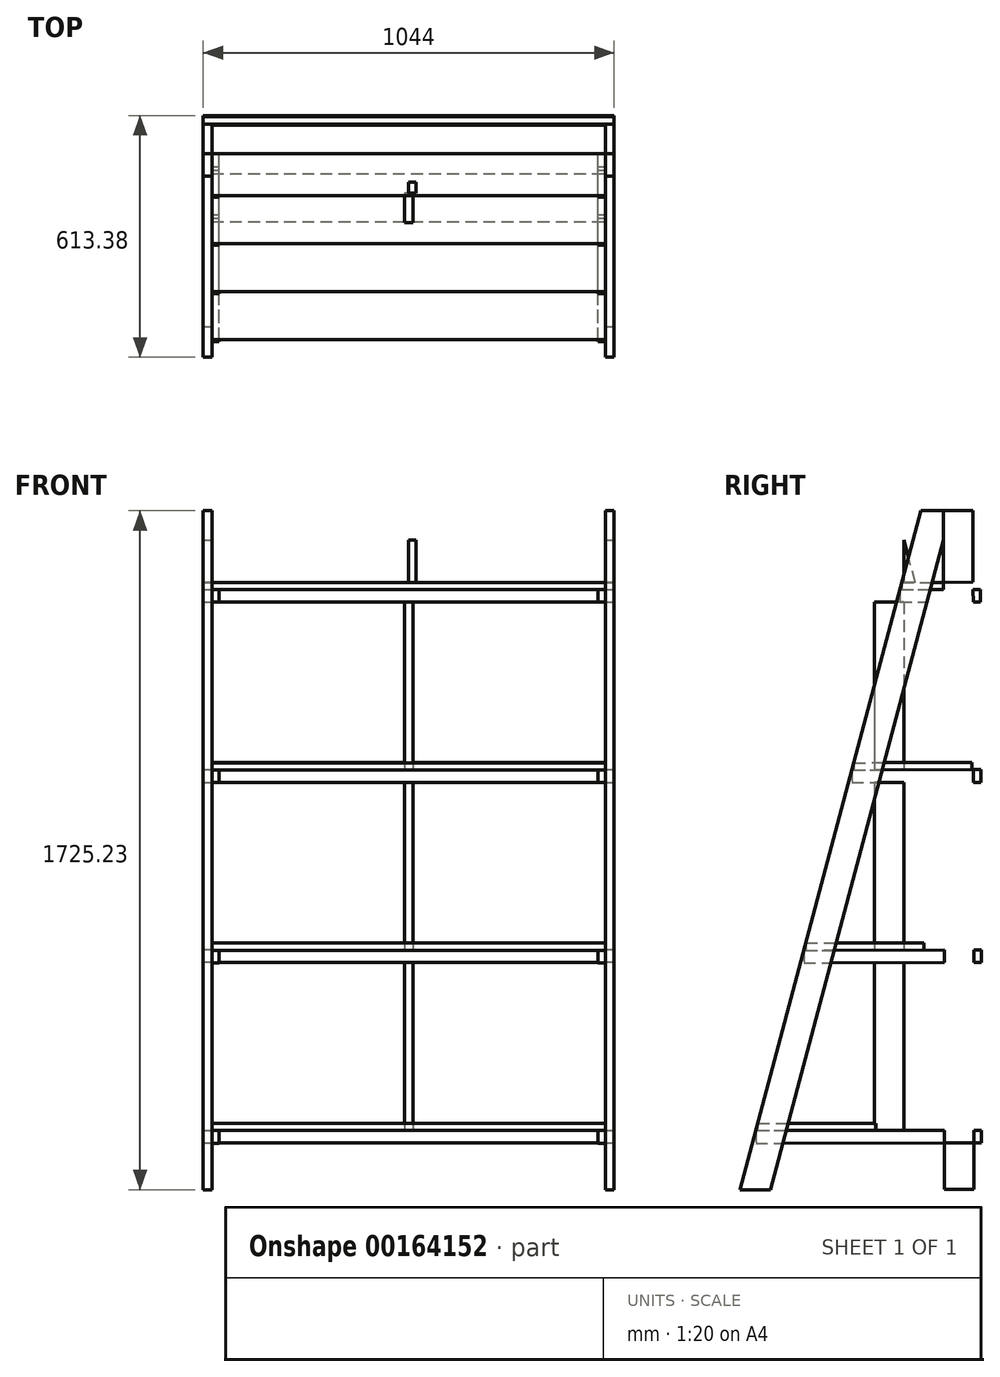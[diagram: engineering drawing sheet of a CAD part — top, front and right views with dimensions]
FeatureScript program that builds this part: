
annotation { "Feature Type Name" : "Feature", "Feature Type Description" : "" }
export const myFeature = defineFeature(function(context is Context, id is Id, definition is map)
    precondition{}
    {
        {
            var Q0;
            Q0=qCreatedBy(makeId("Right.planeOp"),FACE);
            var sketch = newSketch(context, id + "F0", { "sketchPlane" : qUnion([Q0])});
            skLineSegment(sketch, "E0.bottom", {"start": v(-125, 862.14) * mm, "end": v(-50, 862.14) * mm});
            skLineSegment(sketch, "E0.top", {"start": v(-125, -862.14) * mm, "end": v(-50, -862.14) * mm});
            skLineSegment(sketch, "E0.left", {"start": v(-125, 862.14) * mm, "end": v(-125, -862.14) * mm});
            skLineSegment(sketch, "E0.right", {"start": v(-50, 862.14) * mm, "end": v(-50, -862.14) * mm});
            skLineSegment(sketch, "E1", {"start": v(-50, 862.14) * mm, "end": v(7.55, 862.14) * mm});
            skLineSegment(sketch, "E2", {"start": v(7.55, 862.14) * mm, "end": v(469.57, -862.14) * mm});
            skLineSegment(sketch, "E3", {"start": v(469.57, -862.14) * mm, "end": v(391.92, -862.14) * mm});
            skLineSegment(sketch, "E4", {"start": v(391.92, -862.14) * mm, "end": v(-50, 787.14) * mm});
            skLineSegment(sketch, "E5", {"start": v(469.57, -862.14) * mm, "end": v(397.12, -881.55) * mm, "construction": true});
            skLineSegment(sketch, "E6", {"start": v(397.12, -881.55) * mm, "end": v(391.92, -862.14) * mm, "construction": true});
            skLineSegment(sketch, "E7", {"start": v(391.92, -862.14) * mm, "end": v(397.12, -881.55) * mm, "construction": true});
            skLineSegment(sketch, "E8", {"start": v(-50, 787.14) * mm, "end": v(-68.75, 857.12) * mm, "construction": true});
            skLineSegment(sketch, "E9", {"start": v(3.7, 876.53) * mm, "end": v(7.55, 862.14) * mm, "construction": true});
            skLineSegment(sketch, "E10", {"start": v(-68.75, 857.12) * mm, "end": v(-50, 862.14) * mm, "construction": true});
            skLineSegment(sketch, "E11", {"start": v(-50, 862.14) * mm, "end": v(3.7, 876.53) * mm, "construction": true});
            skPoint(sketch, "E12", {"position": v(-50, 0) * mm});
            skLineSegment(sketch, "E13", {"start": v(-50, 0) * mm, "end": v(0, 0) * mm, "construction": true});
            skLineSegment(sketch, "E14", {"start": v(-125, -712.14) * mm, "end": v(429.38, -712.14) * mm, "construction": true});
            skLineSegment(sketch, "E15.bottom", {"start": v(424.55, -694.14) * mm, "end": v(124.55, -694.14) * mm});
            skLineSegment(sketch, "E15.top", {"start": v(424.55, -712.14) * mm, "end": v(124.55, -712.14) * mm});
            skLineSegment(sketch, "E15.left", {"start": v(424.55, -694.14) * mm, "end": v(424.55, -712.14) * mm});
            skLineSegment(sketch, "E15.right", {"start": v(124.55, -694.14) * mm, "end": v(124.55, -712.14) * mm});
            skLineSegment(sketch, "E16", {"start": v(-125, -712.14) * mm, "end": v(-125, -254.05) * mm, "construction": true});
            skLineSegment(sketch, "E17", {"start": v(-125, -254.05) * mm, "end": v(306.63, -254.05) * mm, "construction": true});
            skLineSegment(sketch, "E18", {"start": v(-125, -254.05) * mm, "end": v(-125, 204.05) * mm, "construction": true});
            skLineSegment(sketch, "E19", {"start": v(-125, 204.05) * mm, "end": v(183.89, 204.05) * mm, "construction": true});
            skLineSegment(sketch, "E20", {"start": v(-125, 662.14) * mm, "end": v(61.14, 662.14) * mm, "construction": true});
            skLineSegment(sketch, "E21", {"start": v(-125, 662.14) * mm, "end": v(-125, 204.05) * mm, "construction": true});
            skLineSegment(sketch, "E22.bottom", {"start": v(301.8, -236.05) * mm, "end": v(1.8, -236.05) * mm});
            skLineSegment(sketch, "E22.top", {"start": v(301.8, -254.05) * mm, "end": v(1.8, -254.05) * mm});
            skLineSegment(sketch, "E22.left", {"start": v(301.8, -236.05) * mm, "end": v(301.8, -254.05) * mm});
            skLineSegment(sketch, "E22.right", {"start": v(1.8, -236.05) * mm, "end": v(1.8, -254.05) * mm});
            skLineSegment(sketch, "E23.bottom", {"start": v(179.06, 222.05) * mm, "end": v(-120.94, 222.05) * mm});
            skLineSegment(sketch, "E23.top", {"start": v(179.06, 204.05) * mm, "end": v(-120.94, 204.05) * mm});
            skLineSegment(sketch, "E23.left", {"start": v(179.06, 222.05) * mm, "end": v(179.06, 204.05) * mm});
            skLineSegment(sketch, "E23.right", {"start": v(-120.94, 222.05) * mm, "end": v(-120.94, 204.05) * mm});
            skLineSegment(sketch, "E24.bottom", {"start": v(56.32, 680.14) * mm, "end": v(-125, 680.14) * mm});
            skLineSegment(sketch, "E24.top", {"start": v(56.32, 662.14) * mm, "end": v(-125, 662.14) * mm});
            skLineSegment(sketch, "E24.left", {"start": v(56.32, 680.14) * mm, "end": v(56.32, 662.14) * mm});
            skLineSegment(sketch, "E24.right", {"start": v(-125, 680.14) * mm, "end": v(-125, 662.14) * mm});
            skLineSegment(sketch, "E25.bottom", {"start": v(429.38, -712.14) * mm, "end": v(-125, -712.14) * mm});
            skLineSegment(sketch, "E25.top", {"start": v(429.38, -744.14) * mm, "end": v(-125, -744.14) * mm});
            skLineSegment(sketch, "E25.left", {"start": v(429.38, -712.14) * mm, "end": v(429.38, -744.14) * mm});
            skLineSegment(sketch, "E25.right", {"start": v(-125, -712.14) * mm, "end": v(-125, -744.14) * mm});
            skLineSegment(sketch, "E26.bottom", {"start": v(306.63, -254.05) * mm, "end": v(-125, -254.05) * mm});
            skLineSegment(sketch, "E26.top", {"start": v(306.63, -286.05) * mm, "end": v(-125, -286.05) * mm});
            skLineSegment(sketch, "E26.left", {"start": v(306.63, -254.05) * mm, "end": v(306.63, -286.05) * mm});
            skLineSegment(sketch, "E26.right", {"start": v(-125, -254.05) * mm, "end": v(-125, -286.05) * mm});
            skLineSegment(sketch, "E27.bottom", {"start": v(183.89, 204.05) * mm, "end": v(-125, 204.05) * mm});
            skLineSegment(sketch, "E27.top", {"start": v(183.89, 172.05) * mm, "end": v(-125, 172.05) * mm});
            skLineSegment(sketch, "E27.left", {"start": v(183.89, 204.05) * mm, "end": v(183.89, 172.05) * mm});
            skLineSegment(sketch, "E27.right", {"start": v(-125, 204.05) * mm, "end": v(-125, 172.05) * mm});
            skLineSegment(sketch, "E28.bottom", {"start": v(61.14, 662.14) * mm, "end": v(-125, 662.14) * mm});
            skLineSegment(sketch, "E28.top", {"start": v(61.14, 630.14) * mm, "end": v(-125, 630.14) * mm});
            skLineSegment(sketch, "E28.left", {"start": v(61.14, 662.14) * mm, "end": v(61.14, 630.14) * mm});
            skLineSegment(sketch, "E28.right", {"start": v(-125, 662.14) * mm, "end": v(-125, 630.14) * mm});
            skLineSegment(sketch, "E29", {"start": v(0, 1113.68) * mm, "end": v(1.8, -1143.74) * mm, "construction": true});
            skSolve(sketch);
        }
        {
            var Q0;
            {var subQ0=sQuery(id+"F0.wireOp",EDGE,"E27.left");Q0=makeQuery(id+"F0.imprint","IMPRINT",FACE,{"disambiguationData":[TD([[makeQuery(id+"F0.imprint","IMPRINT",EDGE,{"derivedFrom":subQ0}),-1.0]])]});}
            var Q1;
            {var subQ0=sQuery(id+"F0.wireOp",EDGE,"E27.left");Q1=makeQuery(id+"F0.imprint","IMPRINT",FACE,{"disambiguationData":[TD([[makeQuery(id+"F0.imprint","IMPRINT",EDGE,{"derivedFrom":subQ0}),1.0]])]});}
            var Q2;
            {var subQ0=sQuery(id+"F0.wireOp",EDGE,"E23.left");Q2=makeQuery(id+"F0.imprint","IMPRINT",FACE,{"disambiguationData":[TD([[makeQuery(id+"F0.imprint","IMPRINT",EDGE,{"derivedFrom":subQ0}),1.0]])]});}
            var Q3;
            {var subQ5=sQuery(id+"F0.wireOp",EDGE,"E23.left");Q3=makeQuery(id+"F0.imprint","IMPRINT",FACE,{"disambiguationData":[TD([[makeQuery(id+"F0.imprint","IMPRINT",EDGE,{"derivedFrom":subQ5}),-1.0]])]});}
            var Q4;
            {var subQ0=sQuery(id+"F0.wireOp",EDGE,"E28.left");Q4=makeQuery(id+"F0.imprint","IMPRINT",FACE,{"disambiguationData":[TD([[makeQuery(id+"F0.imprint","IMPRINT",EDGE,{"derivedFrom":subQ0}),1.0]])]});}
            var Q5;
            {var subQ0=sQuery(id+"F0.wireOp",EDGE,"E26.left");Q5=makeQuery(id+"F0.imprint","IMPRINT",FACE,{"disambiguationData":[TD([[makeQuery(id+"F0.imprint","IMPRINT",EDGE,{"derivedFrom":subQ0}),1.0]])]});}
            var Q6;
            {var subQ0=sQuery(id+"F0.wireOp",EDGE,"E26.left");Q6=makeQuery(id+"F0.imprint","IMPRINT",FACE,{"disambiguationData":[TD([[makeQuery(id+"F0.imprint","IMPRINT",EDGE,{"derivedFrom":subQ0}),-1.0]])]});}
            var Q7;
            {var subQ5=sQuery(id+"F0.wireOp",EDGE,"E22.left");Q7=makeQuery(id+"F0.imprint","IMPRINT",FACE,{"disambiguationData":[TD([[makeQuery(id+"F0.imprint","IMPRINT",EDGE,{"derivedFrom":subQ5}),-1.0]])]});}
            var Q8;
            {var subQ0=sQuery(id+"F0.wireOp",EDGE,"E22.left");Q8=makeQuery(id+"F0.imprint","IMPRINT",FACE,{"disambiguationData":[TD([[makeQuery(id+"F0.imprint","IMPRINT",EDGE,{"derivedFrom":subQ0}),1.0]])]});}
            var Q9;
            {var subQ4=sQuery(id+"F0.wireOp",EDGE,"E3");Q9=makeQuery(id+"F0.imprint","IMPRINT",FACE,{"disambiguationData":[TD([[makeQuery(id+"F0.imprint","IMPRINT",EDGE,{"derivedFrom":subQ4}),-1.0]])]});}
            var Q10;
            {var subQ4=sQuery(id+"F0.wireOp",EDGE,"E25.left");Q10=makeQuery(id+"F0.imprint","IMPRINT",FACE,{"disambiguationData":[TD([[makeQuery(id+"F0.imprint","IMPRINT",EDGE,{"derivedFrom":subQ4}),-1.0]])]});}
            var Q11;
            {var subQ5=sQuery(id+"F0.wireOp",EDGE,"E15.left");Q11=makeQuery(id+"F0.imprint","IMPRINT",FACE,{"disambiguationData":[TD([[makeQuery(id+"F0.imprint","IMPRINT",EDGE,{"derivedFrom":subQ5}),-1.0]])]});}
            var Q12;
            {var subQ0=sQuery(id+"F0.wireOp",EDGE,"E15.left");Q12=makeQuery(id+"F0.imprint","IMPRINT",FACE,{"disambiguationData":[TD([[makeQuery(id+"F0.imprint","IMPRINT",EDGE,{"derivedFrom":subQ0}),1.0]])]});}
            var Q13;
            {var subQ1=sQuery(id+"F0.wireOp",EDGE,"E2");var subQ3=sQuery(id+"F0.wireOp",EDGE,"q1gE5B2j-BdVa-rHxn-HZzA-WCDaylD2YWi6");var subQ4=makeQuery(id+"F0.imprint","INTERSECT",VERTEX,{"derivedFrom":[subQ1,subQ3]});Q13=makeQuery(id+"F0.imprint","IMPRINT",FACE,{"disambiguationData":[TD([[makeQuery(id+"F0.imprint","IMPRINT",EDGE,{"disambiguationData":[TD([[subQ4,-1.0]])],"derivedFrom":subQ1}),-1.0]])]});}
            var Q14;
            {var subQ0=sQuery(id+"F0.wireOp",EDGE,"E1");Q14=makeQuery(id+"F0.imprint","IMPRINT",FACE,{"disambiguationData":[TD([[makeQuery(id+"F0.imprint","IMPRINT",EDGE,{"derivedFrom":subQ0}),-1.0]])]});}
            var Q15;
            {var subQ5=sQuery(id+"F0.wireOp",EDGE,"E24.left");Q15=makeQuery(id+"F0.imprint","IMPRINT",FACE,{"disambiguationData":[TD([[makeQuery(id+"F0.imprint","IMPRINT",EDGE,{"derivedFrom":subQ5}),-1.0]])]});}
            var Q16;
            {var subQ0=sQuery(id+"F0.wireOp",EDGE,"E28.left");Q16=makeQuery(id+"F0.imprint","IMPRINT",FACE,{"disambiguationData":[TD([[makeQuery(id+"F0.imprint","IMPRINT",EDGE,{"derivedFrom":subQ0}),-1.0]])]});}
            var Q17;
            {var subQ0=sQuery(id+"F0.wireOp",EDGE,"E24.left");Q17=makeQuery(id+"F0.imprint","IMPRINT",FACE,{"disambiguationData":[TD([[makeQuery(id+"F0.imprint","IMPRINT",EDGE,{"derivedFrom":subQ0}),1.0]])]});}
            extrude(context, id + "F1", {"entities" : qUnion([Q0, Q1, Q2, Q3, Q4, Q5, Q6, Q7, Q8, Q9, Q10, Q11, Q12, Q13, Q14, Q15, Q16, Q17]), "depth" : 11 * mm, "hasSecondDirection" : true, "secondDirectionOppositeDirection" : true, "secondDirectionDepth" : 11 * mm});
        }
        {
            var Q0;
            {var subQ4=sQuery(id+"F0.wireOp",EDGE,"E0.bottom");Q0=makeQuery(id+"F0.imprint","IMPRINT",FACE,{"disambiguationData":[TD([[makeQuery(id+"F0.imprint","IMPRINT",EDGE,{"derivedFrom":subQ4}),-1.0]])]});}
            var Q1;
            {var subQ5=sQuery(id+"F0.wireOp",EDGE,"E24.right");Q1=makeQuery(id+"F0.imprint","IMPRINT",FACE,{"disambiguationData":[TD([[makeQuery(id+"F0.imprint","IMPRINT",EDGE,{"derivedFrom":subQ5}),1.0]])]});}
            var Q2;
            {var subQ5=sQuery(id+"F0.wireOp",EDGE,"E23.right");Q2=makeQuery(id+"F0.imprint","IMPRINT",FACE,{"disambiguationData":[TD([[makeQuery(id+"F0.imprint","IMPRINT",EDGE,{"derivedFrom":subQ5}),-1.0]])]});}
            var Q3;
            {var subQ5=sQuery(id+"F0.wireOp",EDGE,"E28.right");Q3=makeQuery(id+"F0.imprint","IMPRINT",FACE,{"disambiguationData":[TD([[makeQuery(id+"F0.imprint","IMPRINT",EDGE,{"derivedFrom":subQ5}),1.0]])]});}
            var Q4;
            {var subQ2=sQuery(id+"F0.wireOp",EDGE,"E27.right");Q4=makeQuery(id+"F0.imprint","IMPRINT",FACE,{"disambiguationData":[TD([[makeQuery(id+"F0.imprint","IMPRINT",EDGE,{"derivedFrom":subQ2}),1.0]])]});}
            var Q5;
            {var subQ5=sQuery(id+"F0.wireOp",EDGE,"E23.right");Q5=makeQuery(id+"F0.imprint","IMPRINT",FACE,{"disambiguationData":[TD([[makeQuery(id+"F0.imprint","IMPRINT",EDGE,{"derivedFrom":subQ5}),1.0]])]});}
            var Q6;
            {var subQ3=sQuery(id+"F0.wireOp",EDGE,"E27.top");var subQ5=sQuery(id+"F0.wireOp",EDGE,"E0.right");var subQ6=makeQuery(id+"F0.imprint","INTERSECT",VERTEX,{"derivedFrom":[subQ5,subQ3]});Q6=makeQuery(id+"F0.imprint","IMPRINT",FACE,{"disambiguationData":[TD([[makeQuery(id+"F0.imprint","IMPRINT",EDGE,{"disambiguationData":[TD([[subQ6,-1.0]])],"derivedFrom":subQ5}),-1.0]])]});}
            var Q7;
            {var subQ5=sQuery(id+"F0.wireOp",EDGE,"E26.right");Q7=makeQuery(id+"F0.imprint","IMPRINT",FACE,{"disambiguationData":[TD([[makeQuery(id+"F0.imprint","IMPRINT",EDGE,{"derivedFrom":subQ5}),1.0]])]});}
            var Q8;
            {var subQ3=sQuery(id+"F0.wireOp",EDGE,"E26.top");var subQ5=sQuery(id+"F0.wireOp",EDGE,"E0.right");var subQ7=makeQuery(id+"F0.imprint","INTERSECT",VERTEX,{"derivedFrom":[subQ5,subQ3]});Q8=makeQuery(id+"F0.imprint","IMPRINT",FACE,{"disambiguationData":[TD([[makeQuery(id+"F0.imprint","IMPRINT",EDGE,{"disambiguationData":[TD([[subQ7,-1.0]])],"derivedFrom":subQ5}),-1.0]])]});}
            var Q9;
            {var subQ5=sQuery(id+"F0.wireOp",EDGE,"E25.right");Q9=makeQuery(id+"F0.imprint","IMPRINT",FACE,{"disambiguationData":[TD([[makeQuery(id+"F0.imprint","IMPRINT",EDGE,{"derivedFrom":subQ5}),1.0]])]});}
            var Q10;
            {var subQ0=sQuery(id+"F0.wireOp",EDGE,"E0.top");Q10=makeQuery(id+"F0.imprint","IMPRINT",FACE,{"disambiguationData":[TD([[makeQuery(id+"F0.imprint","IMPRINT",EDGE,{"derivedFrom":subQ0}),1.0]])]});}
            extrude(context, id + "F2", {"entities" : qUnion([Q0, Q1, Q2, Q3, Q4, Q5, Q6, Q7, Q8, Q9, Q10]), "depth" : 11 * mm, "hasSecondDirection" : true, "secondDirectionOppositeDirection" : true, "secondDirectionDepth" : 11 * mm});
        }
        {
            var Q0;
            Q0=makeQuery(id+"F1.opExtrude","SWEPT_BODY",BODY,{"disambiguationData":[OSD([sQuery(id+"F0.wireOp",EDGE,"E0.bottom"),sQuery(id+"F0.wireOp",EDGE,"E0.top"),sQuery(id+"F0.wireOp",EDGE,"E0.left"),sQuery(id+"F0.wireOp",EDGE,"E0.right"),sQuery(id+"F0.wireOp",EDGE,"E1"),sQuery(id+"F0.wireOp",EDGE,"E2"),sQuery(id+"F0.wireOp",EDGE,"E3"),sQuery(id+"F0.wireOp",EDGE,"E4"),sQuery(id+"F0.wireOp",EDGE,"E24.right"),sQuery(id+"F0.wireOp",EDGE,"E25.right"),sQuery(id+"F0.wireOp",EDGE,"E26.right"),sQuery(id+"F0.wireOp",EDGE,"E27.right"),sQuery(id+"F0.wireOp",EDGE,"E28.right")])]});
            var Q1;
            Q1=makeQuery(id+"F2.opExtrude","SWEPT_BODY",BODY,{"disambiguationData":[OSD([sQuery(id+"F0.wireOp",EDGE,"E0.bottom"),sQuery(id+"F0.wireOp",EDGE,"E0.top"),sQuery(id+"F0.wireOp",EDGE,"E0.left"),sQuery(id+"F0.wireOp",EDGE,"E0.right"),sQuery(id+"F0.wireOp",EDGE,"E24.right"),sQuery(id+"F0.wireOp",EDGE,"E25.right"),sQuery(id+"F0.wireOp",EDGE,"E26.right"),sQuery(id+"F0.wireOp",EDGE,"E27.right"),sQuery(id+"F0.wireOp",EDGE,"E28.right")])]});
            transform(context, id + "F3", {"entities" : qUnion([Q0, Q1]), "transformType" : TransformType.TRANSLATION_3D, "dx" : 511 * mm, "dy" : 0 * mm, "dz" : 0 * mm, "makeCopy" : false});
        }
        {
            var Q0;
            Q0=makeQuery(id+"F1.opExtrude","SWEPT_BODY",BODY,{"disambiguationData":[OSD([sQuery(id+"F0.wireOp",EDGE,"E0.bottom"),sQuery(id+"F0.wireOp",EDGE,"E0.top"),sQuery(id+"F0.wireOp",EDGE,"E0.left"),sQuery(id+"F0.wireOp",EDGE,"E0.right"),sQuery(id+"F0.wireOp",EDGE,"E1"),sQuery(id+"F0.wireOp",EDGE,"E2"),sQuery(id+"F0.wireOp",EDGE,"E3"),sQuery(id+"F0.wireOp",EDGE,"E4"),sQuery(id+"F0.wireOp",EDGE,"E24.right"),sQuery(id+"F0.wireOp",EDGE,"E25.right"),sQuery(id+"F0.wireOp",EDGE,"E26.right"),sQuery(id+"F0.wireOp",EDGE,"E27.right"),sQuery(id+"F0.wireOp",EDGE,"E28.right")])]});
            var Q1;
            Q1=makeQuery(id+"F2.opExtrude","SWEPT_BODY",BODY,{"disambiguationData":[OSD([sQuery(id+"F0.wireOp",EDGE,"E0.bottom"),sQuery(id+"F0.wireOp",EDGE,"E0.top"),sQuery(id+"F0.wireOp",EDGE,"E0.left"),sQuery(id+"F0.wireOp",EDGE,"E0.right"),sQuery(id+"F0.wireOp",EDGE,"E24.right"),sQuery(id+"F0.wireOp",EDGE,"E25.right"),sQuery(id+"F0.wireOp",EDGE,"E26.right"),sQuery(id+"F0.wireOp",EDGE,"E27.right"),sQuery(id+"F0.wireOp",EDGE,"E28.right")])]});
            transform(context, id + "F4", {"entities" : qUnion([Q0, Q1]), "transformType" : TransformType.TRANSLATION_3D, "dx" : -1022 * mm, "dy" : 0 * mm, "dz" : 0 * mm, "makeCopy" : true});
        }
        {
            var Q0;
            {var subQ2=sQuery(id+"F0.wireOp",EDGE,"E0.right");var subQ6=sQuery(id+"F0.wireOp",EDGE,"E25.top");var subQ8=makeQuery(id+"F0.imprint","INTERSECT",VERTEX,{"derivedFrom":[subQ2,subQ6]});Q0=makeQuery(id+"F0.imprint","IMPRINT",FACE,{"disambiguationData":[TD([[makeQuery(id+"F0.imprint","IMPRINT",EDGE,{"disambiguationData":[TD([[subQ8,1.0]])],"derivedFrom":subQ2}),1.0]])]});}
            var Q1;
            {var subQ5=sQuery(id+"F0.wireOp",EDGE,"E25.right");Q1=makeQuery(id+"F0.imprint","IMPRINT",FACE,{"disambiguationData":[TD([[makeQuery(id+"F0.imprint","IMPRINT",EDGE,{"derivedFrom":subQ5}),1.0]])]});}
            var Q2;
            {var subQ4=sQuery(id+"F0.wireOp",EDGE,"E25.left");Q2=makeQuery(id+"F0.imprint","IMPRINT",FACE,{"disambiguationData":[TD([[makeQuery(id+"F0.imprint","IMPRINT",EDGE,{"derivedFrom":subQ4}),-1.0]])]});}
            var Q3;
            {var subQ0=sQuery(id+"F0.wireOp",EDGE,"E26.left");Q3=makeQuery(id+"F0.imprint","IMPRINT",FACE,{"disambiguationData":[TD([[makeQuery(id+"F0.imprint","IMPRINT",EDGE,{"derivedFrom":subQ0}),-1.0]])]});}
            var Q4;
            {var subQ0=sQuery(id+"F0.wireOp",EDGE,"E26.bottom");var subQ2=sQuery(id+"F0.wireOp",EDGE,"E0.right");var subQ3=makeQuery(id+"F0.imprint","INTERSECT",VERTEX,{"derivedFrom":[subQ2,subQ0]});Q4=makeQuery(id+"F0.imprint","IMPRINT",FACE,{"disambiguationData":[TD([[makeQuery(id+"F0.imprint","IMPRINT",EDGE,{"disambiguationData":[TD([[subQ3,-1.0]])],"derivedFrom":subQ2}),1.0]])]});}
            var Q5;
            {var subQ5=sQuery(id+"F0.wireOp",EDGE,"E26.right");Q5=makeQuery(id+"F0.imprint","IMPRINT",FACE,{"disambiguationData":[TD([[makeQuery(id+"F0.imprint","IMPRINT",EDGE,{"derivedFrom":subQ5}),1.0]])]});}
            var Q6;
            {var subQ2=sQuery(id+"F0.wireOp",EDGE,"E27.right");Q6=makeQuery(id+"F0.imprint","IMPRINT",FACE,{"disambiguationData":[TD([[makeQuery(id+"F0.imprint","IMPRINT",EDGE,{"derivedFrom":subQ2}),1.0]])]});}
            var Q7;
            {var subQ0=sQuery(id+"F0.wireOp",EDGE,"E27.bottom");var subQ1=sQuery(id+"F0.wireOp",EDGE,"E0.right");var subQ2=makeQuery(id+"F0.imprint","INTERSECT",VERTEX,{"derivedFrom":[subQ1,subQ0]});Q7=makeQuery(id+"F0.imprint","IMPRINT",FACE,{"disambiguationData":[TD([[makeQuery(id+"F0.imprint","IMPRINT",EDGE,{"disambiguationData":[TD([[subQ2,-1.0]])],"derivedFrom":subQ1}),1.0]])]});}
            var Q8;
            {var subQ0=sQuery(id+"F0.wireOp",EDGE,"E27.left");Q8=makeQuery(id+"F0.imprint","IMPRINT",FACE,{"disambiguationData":[TD([[makeQuery(id+"F0.imprint","IMPRINT",EDGE,{"derivedFrom":subQ0}),-1.0]])]});}
            var Q9;
            {var subQ5=sQuery(id+"F0.wireOp",EDGE,"E28.right");Q9=makeQuery(id+"F0.imprint","IMPRINT",FACE,{"disambiguationData":[TD([[makeQuery(id+"F0.imprint","IMPRINT",EDGE,{"derivedFrom":subQ5}),1.0]])]});}
            var Q10;
            {var subQ0=sQuery(id+"F0.wireOp",EDGE,"E28.bottom");var subQ1=sQuery(id+"F0.wireOp",EDGE,"E0.right");var subQ2=makeQuery(id+"F0.imprint","INTERSECT",VERTEX,{"derivedFrom":[subQ1,subQ0]});Q10=makeQuery(id+"F0.imprint","IMPRINT",FACE,{"disambiguationData":[TD([[makeQuery(id+"F0.imprint","IMPRINT",EDGE,{"disambiguationData":[TD([[subQ2,-1.0]])],"derivedFrom":subQ1}),1.0]])]});}
            var Q11;
            {var subQ0=sQuery(id+"F0.wireOp",EDGE,"E28.left");Q11=makeQuery(id+"F0.imprint","IMPRINT",FACE,{"disambiguationData":[TD([[makeQuery(id+"F0.imprint","IMPRINT",EDGE,{"derivedFrom":subQ0}),-1.0]])]});}
            extrude(context, id + "F5", {"entities" : qUnion([Q0, Q1, Q2, Q3, Q4, Q5, Q6, Q7, Q8, Q9, Q10, Q11]), "depth" : 19 * mm});
        }
        {
            var Q0;
            Q0=makeQuery(id+"F5.opExtrude","SWEPT_BODY",BODY,{"disambiguationData":[OSD([sQuery(id+"F0.wireOp",EDGE,"E28.bottom"),sQuery(id+"F0.wireOp",EDGE,"E28.top"),sQuery(id+"F0.wireOp",EDGE,"E28.left"),sQuery(id+"F0.wireOp",EDGE,"E28.right")])]});
            var Q1;
            Q1=makeQuery(id+"F5.opExtrude","SWEPT_BODY",BODY,{"disambiguationData":[OSD([sQuery(id+"F0.wireOp",EDGE,"E27.bottom"),sQuery(id+"F0.wireOp",EDGE,"E27.top"),sQuery(id+"F0.wireOp",EDGE,"E27.left"),sQuery(id+"F0.wireOp",EDGE,"E27.right")])]});
            var Q2;
            Q2=makeQuery(id+"F5.opExtrude","SWEPT_BODY",BODY,{"disambiguationData":[OSD([sQuery(id+"F0.wireOp",EDGE,"E26.bottom"),sQuery(id+"F0.wireOp",EDGE,"E26.top"),sQuery(id+"F0.wireOp",EDGE,"E26.left"),sQuery(id+"F0.wireOp",EDGE,"E26.right")])]});
            var Q3;
            Q3=makeQuery(id+"F5.opExtrude","SWEPT_BODY",BODY,{"disambiguationData":[OSD([sQuery(id+"F0.wireOp",EDGE,"E25.bottom"),sQuery(id+"F0.wireOp",EDGE,"E25.top"),sQuery(id+"F0.wireOp",EDGE,"E25.left"),sQuery(id+"F0.wireOp",EDGE,"E25.right")])]});
            transform(context, id + "F6", {"entities" : qUnion([Q0, Q1, Q2, Q3]), "transformType" : TransformType.TRANSLATION_3D, "dx" : -500 * mm, "dy" : 0 * mm, "dz" : 0 * mm, "makeCopy" : false});
        }
        {
            var Q0;
            Q0=makeQuery(id+"F5.opExtrude","SWEPT_BODY",BODY,{"disambiguationData":[OSD([sQuery(id+"F0.wireOp",EDGE,"E27.bottom"),sQuery(id+"F0.wireOp",EDGE,"E27.top"),sQuery(id+"F0.wireOp",EDGE,"E27.left"),sQuery(id+"F0.wireOp",EDGE,"E27.right")])]});
            var Q1;
            Q1=makeQuery(id+"F5.opExtrude","SWEPT_BODY",BODY,{"disambiguationData":[OSD([sQuery(id+"F0.wireOp",EDGE,"E28.bottom"),sQuery(id+"F0.wireOp",EDGE,"E28.top"),sQuery(id+"F0.wireOp",EDGE,"E28.left"),sQuery(id+"F0.wireOp",EDGE,"E28.right")])]});
            var Q2;
            Q2=makeQuery(id+"F5.opExtrude","SWEPT_BODY",BODY,{"disambiguationData":[OSD([sQuery(id+"F0.wireOp",EDGE,"E26.bottom"),sQuery(id+"F0.wireOp",EDGE,"E26.top"),sQuery(id+"F0.wireOp",EDGE,"E26.left"),sQuery(id+"F0.wireOp",EDGE,"E26.right")])]});
            var Q3;
            Q3=makeQuery(id+"F5.opExtrude","SWEPT_BODY",BODY,{"disambiguationData":[OSD([sQuery(id+"F0.wireOp",EDGE,"E25.bottom"),sQuery(id+"F0.wireOp",EDGE,"E25.top"),sQuery(id+"F0.wireOp",EDGE,"E25.left"),sQuery(id+"F0.wireOp",EDGE,"E25.right")])]});
            transform(context, id + "F7", {"entities" : qUnion([Q0, Q1, Q2, Q3]), "transformType" : TransformType.TRANSLATION_3D, "dx" : 981 * mm, "dy" : 0 * mm, "dz" : 0 * mm, "makeCopy" : true});
        }
        {
            var Q0;
            {var subQ0=sQuery(id+"F0.wireOp",EDGE,"E24.bottom");var subQ1=sQuery(id+"F0.wireOp",EDGE,"E0.right");var subQ2=makeQuery(id+"F0.imprint","INTERSECT",VERTEX,{"derivedFrom":[subQ1,subQ0]});Q0=makeQuery(id+"F0.imprint","IMPRINT",FACE,{"disambiguationData":[TD([[makeQuery(id+"F0.imprint","IMPRINT",EDGE,{"disambiguationData":[TD([[subQ2,-1.0]])],"derivedFrom":subQ1}),1.0]])]});}
            var Q1;
            {var subQ5=sQuery(id+"F0.wireOp",EDGE,"E24.right");Q1=makeQuery(id+"F0.imprint","IMPRINT",FACE,{"disambiguationData":[TD([[makeQuery(id+"F0.imprint","IMPRINT",EDGE,{"derivedFrom":subQ5}),1.0]])]});}
            var Q2;
            {var subQ5=sQuery(id+"F0.wireOp",EDGE,"E24.left");Q2=makeQuery(id+"F0.imprint","IMPRINT",FACE,{"disambiguationData":[TD([[makeQuery(id+"F0.imprint","IMPRINT",EDGE,{"derivedFrom":subQ5}),-1.0]])]});}
            var Q3;
            {var subQ5=sQuery(id+"F0.wireOp",EDGE,"E23.left");Q3=makeQuery(id+"F0.imprint","IMPRINT",FACE,{"disambiguationData":[TD([[makeQuery(id+"F0.imprint","IMPRINT",EDGE,{"derivedFrom":subQ5}),-1.0]])]});}
            var Q4;
            {var subQ0=sQuery(id+"F0.wireOp",EDGE,"E23.bottom");var subQ1=sQuery(id+"F0.wireOp",EDGE,"E0.right");var subQ2=makeQuery(id+"F0.imprint","INTERSECT",VERTEX,{"derivedFrom":[subQ1,subQ0]});Q4=makeQuery(id+"F0.imprint","IMPRINT",FACE,{"disambiguationData":[TD([[makeQuery(id+"F0.imprint","IMPRINT",EDGE,{"disambiguationData":[TD([[subQ2,-1.0]])],"derivedFrom":subQ1}),1.0]])]});}
            var Q5;
            {var subQ5=sQuery(id+"F0.wireOp",EDGE,"E23.right");Q5=makeQuery(id+"F0.imprint","IMPRINT",FACE,{"disambiguationData":[TD([[makeQuery(id+"F0.imprint","IMPRINT",EDGE,{"derivedFrom":subQ5}),1.0]])]});}
            var Q6;
            {var subQ5=sQuery(id+"F0.wireOp",EDGE,"E22.right");Q6=makeQuery(id+"F0.imprint","IMPRINT",FACE,{"disambiguationData":[TD([[makeQuery(id+"F0.imprint","IMPRINT",EDGE,{"derivedFrom":subQ5}),1.0]])]});}
            var Q7;
            {var subQ5=sQuery(id+"F0.wireOp",EDGE,"E22.left");Q7=makeQuery(id+"F0.imprint","IMPRINT",FACE,{"disambiguationData":[TD([[makeQuery(id+"F0.imprint","IMPRINT",EDGE,{"derivedFrom":subQ5}),-1.0]])]});}
            var Q8;
            {var subQ5=sQuery(id+"F0.wireOp",EDGE,"E15.right");Q8=makeQuery(id+"F0.imprint","IMPRINT",FACE,{"disambiguationData":[TD([[makeQuery(id+"F0.imprint","IMPRINT",EDGE,{"derivedFrom":subQ5}),1.0]])]});}
            var Q9;
            {var subQ5=sQuery(id+"F0.wireOp",EDGE,"E15.left");Q9=makeQuery(id+"F0.imprint","IMPRINT",FACE,{"disambiguationData":[TD([[makeQuery(id+"F0.imprint","IMPRINT",EDGE,{"derivedFrom":subQ5}),-1.0]])]});}
            extrude(context, id + "F8", {"entities" : qUnion([Q0, Q1, Q2, Q3, Q4, Q5, Q6, Q7, Q8, Q9]), "depth" : 500 * mm, "hasSecondDirection" : true, "secondDirectionOppositeDirection" : true, "secondDirectionDepth" : 500 * mm});
        }
        {
            var Q0;
            Q0=qCreatedBy(makeId("Front.planeOp"),FACE);
            var sketch = newSketch(context, id + "F9", { "sketchPlane" : qUnion([Q0])});
            skLineSegment(sketch, "E30.bottom", {"start": v(522, 662.14) * mm, "end": v(-522, 662.14) * mm});
            skLineSegment(sketch, "E30.top", {"start": v(522, 630.14) * mm, "end": v(-522, 630.14) * mm});
            skLineSegment(sketch, "E30.left", {"start": v(522, 662.14) * mm, "end": v(522, 630.14) * mm});
            skLineSegment(sketch, "E30.right", {"start": v(-522, 662.14) * mm, "end": v(-522, 630.14) * mm});
            skLineSegment(sketch, "E31.bottom", {"start": v(522, 204.05) * mm, "end": v(-522, 204.05) * mm});
            skLineSegment(sketch, "E31.top", {"start": v(522, 172.05) * mm, "end": v(-522, 172.05) * mm});
            skLineSegment(sketch, "E31.left", {"start": v(522, 204.05) * mm, "end": v(522, 172.05) * mm});
            skLineSegment(sketch, "E31.right", {"start": v(-522, 204.05) * mm, "end": v(-522, 172.05) * mm});
            skLineSegment(sketch, "E32.bottom", {"start": v(522, -712.14) * mm, "end": v(-522, -712.14) * mm});
            skLineSegment(sketch, "E32.top", {"start": v(522, -744.14) * mm, "end": v(-522, -744.14) * mm});
            skLineSegment(sketch, "E32.left", {"start": v(522, -712.14) * mm, "end": v(522, -744.14) * mm});
            skLineSegment(sketch, "E32.right", {"start": v(-522, -712.14) * mm, "end": v(-522, -744.14) * mm});
            skLineSegment(sketch, "E33", {"start": v(0, -862.14) * mm, "end": v(0, 862.14) * mm, "construction": true});
            skPoint(sketch, "E34", {"position": v(0, 630.14) * mm});
            skPoint(sketch, "E35", {"position": v(0, -744.14) * mm});
            skPoint(sketch, "E36", {"position": v(0, 172.05) * mm});
            skLineSegment(sketch, "E37.bottom", {"start": v(-522, -254.05) * mm, "end": v(522, -254.05) * mm});
            skLineSegment(sketch, "E37.top", {"start": v(-522, -286.05) * mm, "end": v(522, -286.05) * mm});
            skLineSegment(sketch, "E37.left", {"start": v(-522, -254.05) * mm, "end": v(-522, -286.05) * mm});
            skLineSegment(sketch, "E37.right", {"start": v(522, -254.05) * mm, "end": v(522, -286.05) * mm});
            skPoint(sketch, "E38", {"position": v(0, -286.05) * mm});
            skLineSegment(sketch, "E39", {"start": v(276.07, 630.14) * mm, "end": v(276.07, 204.05) * mm, "construction": true});
            skLineSegment(sketch, "E40", {"start": v(276.07, 172.05) * mm, "end": v(276.07, -254.05) * mm, "construction": true});
            skLineSegment(sketch, "E41", {"start": v(276.07, -286.05) * mm, "end": v(276.07, -712.14) * mm, "construction": true});
            skLineSegment(sketch, "E42", {"start": v(-522, 630.14) * mm, "end": v(442.8, 204.05) * mm});
            skLineSegment(sketch, "E43", {"start": v(442.8, 204.05) * mm, "end": v(522, 204.05) * mm});
            skLineSegment(sketch, "E44", {"start": v(522, 204.05) * mm, "end": v(-442.8, 630.14) * mm});
            skLineSegment(sketch, "E45", {"start": v(-442.8, 630.14) * mm, "end": v(-522, 630.14) * mm});
            skLineSegment(sketch, "E46", {"start": v(522, 172.05) * mm, "end": v(-442.8, -254.05) * mm});
            skLineSegment(sketch, "E47", {"start": v(-442.8, -254.05) * mm, "end": v(-522, -254.05) * mm});
            skLineSegment(sketch, "E48", {"start": v(-522, -254.05) * mm, "end": v(442.8, 172.05) * mm});
            skLineSegment(sketch, "E49", {"start": v(442.8, 172.05) * mm, "end": v(522, 172.05) * mm});
            skLineSegment(sketch, "E50", {"start": v(-522, -286.05) * mm, "end": v(442.8, -712.14) * mm});
            skLineSegment(sketch, "E51", {"start": v(442.8, -712.14) * mm, "end": v(522, -712.14) * mm});
            skLineSegment(sketch, "E52", {"start": v(522, -712.14) * mm, "end": v(-442.8, -286.05) * mm});
            skLineSegment(sketch, "E53", {"start": v(-442.8, -286.05) * mm, "end": v(-522, -286.05) * mm});
            skSolve(sketch);
        }
        {
            var Q0;
            Q0=makeQuery(id+"F9.imprint","IMPRINT",FACE,{"disambiguationData":[TD([[makeQuery(id+"F9.imprint","IMPRINT",EDGE,{"derivedFrom":sQuery(id+"F9.wireOp",EDGE,"E30.bottom")}),1.0]])]});
            var Q1;
            Q1=makeQuery(id+"F9.imprint","IMPRINT",FACE,{"disambiguationData":[TD([[makeQuery(id+"F9.imprint","IMPRINT",EDGE,{"derivedFrom":sQuery(id+"F9.wireOp",EDGE,"E32.bottom")}),1.0]])]});
            var Q2;
            Q2=makeQuery(id+"F9.imprint","IMPRINT",FACE,{"disambiguationData":[TD([[makeQuery(id+"F9.imprint","IMPRINT",EDGE,{"derivedFrom":sQuery(id+"F9.wireOp",EDGE,"E31.bottom")}),1.0]])]});
            var Q3;
            Q3=makeQuery(id+"F9.imprint","IMPRINT",FACE,{"disambiguationData":[TD([[makeQuery(id+"F9.imprint","IMPRINT",EDGE,{"derivedFrom":sQuery(id+"F9.wireOp",EDGE,"E37.bottom")}),-1.0]])]});
            extrude(context, id + "F10", {"entities" : qUnion([Q0, Q1, Q2, Q3]), "depth" : 19 * mm});
        }
        {
            var Q0;
            Q0=makeQuery(id+"F10.opExtrude","SWEPT_BODY",BODY,{"disambiguationData":[OSD([sQuery(id+"F9.wireOp",EDGE,"E30.bottom"),sQuery(id+"F9.wireOp",EDGE,"E30.top"),sQuery(id+"F9.wireOp",EDGE,"E30.left"),sQuery(id+"F9.wireOp",EDGE,"E30.right")])]});
            var Q1;
            Q1=makeQuery(id+"F10.opExtrude","SWEPT_BODY",BODY,{"disambiguationData":[OSD([sQuery(id+"F9.wireOp",EDGE,"E31.bottom"),sQuery(id+"F9.wireOp",EDGE,"E31.top"),sQuery(id+"F9.wireOp",EDGE,"E31.left"),sQuery(id+"F9.wireOp",EDGE,"E31.right")])]});
            var Q2;
            Q2=makeQuery(id+"F10.opExtrude","SWEPT_BODY",BODY,{"disambiguationData":[OSD([sQuery(id+"F9.wireOp",EDGE,"E37.bottom"),sQuery(id+"F9.wireOp",EDGE,"E37.top"),sQuery(id+"F9.wireOp",EDGE,"E37.left"),sQuery(id+"F9.wireOp",EDGE,"E37.right")])]});
            var Q3;
            Q3=makeQuery(id+"F10.opExtrude","SWEPT_BODY",BODY,{"disambiguationData":[OSD([sQuery(id+"F9.wireOp",EDGE,"E32.bottom"),sQuery(id+"F9.wireOp",EDGE,"E32.top"),sQuery(id+"F9.wireOp",EDGE,"E32.left"),sQuery(id+"F9.wireOp",EDGE,"E32.right")])]});
            transform(context, id + "F11", {"entities" : qUnion([Q0, Q1, Q2, Q3]), "transformType" : TransformType.TRANSLATION_3D, "dx" : 0 * mm, "dy" : -125 * mm, "dz" : 0 * mm, "makeCopy" : false});
        }
        {
            var Q0;
            Q0=makeQuery(id+"F1.opExtrude","SWEPT_BODY",BODY,{"disambiguationData":[OSD([sQuery(id+"F0.wireOp",EDGE,"E0.right"),sQuery(id+"F0.wireOp",EDGE,"E1"),sQuery(id+"F0.wireOp",EDGE,"E2"),sQuery(id+"F0.wireOp",EDGE,"E3"),sQuery(id+"F0.wireOp",EDGE,"E4")])]});
            var Q1;
            Q1=makeQuery(id+"F2.opExtrude","SWEPT_BODY",BODY,{"disambiguationData":[OSD([sQuery(id+"F0.wireOp",EDGE,"E0.bottom"),sQuery(id+"F0.wireOp",EDGE,"E0.top"),sQuery(id+"F0.wireOp",EDGE,"E0.left"),sQuery(id+"F0.wireOp",EDGE,"E0.right"),sQuery(id+"F0.wireOp",EDGE,"E24.right"),sQuery(id+"F0.wireOp",EDGE,"E25.right"),sQuery(id+"F0.wireOp",EDGE,"E26.right"),sQuery(id+"F0.wireOp",EDGE,"E27.right"),sQuery(id+"F0.wireOp",EDGE,"E28.right")])]});
            var Q2;
            Q2=makeQuery(id+"F4.opPattern","COPY",BODY,{"derivedFrom":makeQuery(id+"F1.opExtrude","SWEPT_BODY",BODY,{"disambiguationData":[OSD([sQuery(id+"F0.wireOp",EDGE,"E0.right"),sQuery(id+"F0.wireOp",EDGE,"E1"),sQuery(id+"F0.wireOp",EDGE,"E2"),sQuery(id+"F0.wireOp",EDGE,"E3"),sQuery(id+"F0.wireOp",EDGE,"E4")])]}),"instanceName":"1"});
            var Q3;
            Q3=makeQuery(id+"F4.opPattern","COPY",BODY,{"derivedFrom":makeQuery(id+"F2.opExtrude","SWEPT_BODY",BODY,{"disambiguationData":[OSD([sQuery(id+"F0.wireOp",EDGE,"E0.bottom"),sQuery(id+"F0.wireOp",EDGE,"E0.top"),sQuery(id+"F0.wireOp",EDGE,"E0.left"),sQuery(id+"F0.wireOp",EDGE,"E0.right"),sQuery(id+"F0.wireOp",EDGE,"E24.right"),sQuery(id+"F0.wireOp",EDGE,"E25.right"),sQuery(id+"F0.wireOp",EDGE,"E26.right"),sQuery(id+"F0.wireOp",EDGE,"E27.right"),sQuery(id+"F0.wireOp",EDGE,"E28.right")])]}),"instanceName":"1"});
            var Q4;
            Q4=makeQuery(id+"F5.opExtrude","SWEPT_BODY",BODY,{"disambiguationData":[OSD([sQuery(id+"F0.wireOp",EDGE,"E25.bottom"),sQuery(id+"F0.wireOp",EDGE,"E25.top"),sQuery(id+"F0.wireOp",EDGE,"E25.left"),sQuery(id+"F0.wireOp",EDGE,"E25.right")])]});
            var Q5;
            Q5=makeQuery(id+"F5.opExtrude","SWEPT_BODY",BODY,{"disambiguationData":[OSD([sQuery(id+"F0.wireOp",EDGE,"E26.bottom"),sQuery(id+"F0.wireOp",EDGE,"E26.top"),sQuery(id+"F0.wireOp",EDGE,"E26.left"),sQuery(id+"F0.wireOp",EDGE,"E26.right")])]});
            var Q6;
            Q6=makeQuery(id+"F7.opPattern","COPY",BODY,{"derivedFrom":makeQuery(id+"F5.opExtrude","SWEPT_BODY",BODY,{"disambiguationData":[OSD([sQuery(id+"F0.wireOp",EDGE,"E25.bottom"),sQuery(id+"F0.wireOp",EDGE,"E25.top"),sQuery(id+"F0.wireOp",EDGE,"E25.left"),sQuery(id+"F0.wireOp",EDGE,"E25.right")])]}),"instanceName":"1"});
            var Q7;
            Q7=makeQuery(id+"F5.opExtrude","SWEPT_BODY",BODY,{"disambiguationData":[OSD([sQuery(id+"F0.wireOp",EDGE,"E28.bottom"),sQuery(id+"F0.wireOp",EDGE,"E28.top"),sQuery(id+"F0.wireOp",EDGE,"E28.left"),sQuery(id+"F0.wireOp",EDGE,"E28.right")])]});
            var Q8;
            Q8=makeQuery(id+"F7.opPattern","COPY",BODY,{"derivedFrom":makeQuery(id+"F5.opExtrude","SWEPT_BODY",BODY,{"disambiguationData":[OSD([sQuery(id+"F0.wireOp",EDGE,"E26.bottom"),sQuery(id+"F0.wireOp",EDGE,"E26.top"),sQuery(id+"F0.wireOp",EDGE,"E26.left"),sQuery(id+"F0.wireOp",EDGE,"E26.right")])]}),"instanceName":"1"});
            var Q9;
            Q9=makeQuery(id+"F7.opPattern","COPY",BODY,{"derivedFrom":makeQuery(id+"F5.opExtrude","SWEPT_BODY",BODY,{"disambiguationData":[OSD([sQuery(id+"F0.wireOp",EDGE,"E27.bottom"),sQuery(id+"F0.wireOp",EDGE,"E27.top"),sQuery(id+"F0.wireOp",EDGE,"E27.left"),sQuery(id+"F0.wireOp",EDGE,"E27.right")])]}),"instanceName":"1"});
            var Q10;
            Q10=makeQuery(id+"F8.opExtrude","SWEPT_BODY",BODY,{"disambiguationData":[OSD([sQuery(id+"F0.wireOp",EDGE,"E15.bottom"),sQuery(id+"F0.wireOp",EDGE,"E15.left"),sQuery(id+"F0.wireOp",EDGE,"E15.right"),sQuery(id+"F0.wireOp",EDGE,"E25.bottom")])]});
            var Q11;
            Q11=makeQuery(id+"F7.opPattern","COPY",BODY,{"derivedFrom":makeQuery(id+"F5.opExtrude","SWEPT_BODY",BODY,{"disambiguationData":[OSD([sQuery(id+"F0.wireOp",EDGE,"E28.bottom"),sQuery(id+"F0.wireOp",EDGE,"E28.top"),sQuery(id+"F0.wireOp",EDGE,"E28.left"),sQuery(id+"F0.wireOp",EDGE,"E28.right")])]}),"instanceName":"1"});
            var Q12;
            Q12=makeQuery(id+"F8.opExtrude","SWEPT_BODY",BODY,{"disambiguationData":[OSD([sQuery(id+"F0.wireOp",EDGE,"E22.bottom"),sQuery(id+"F0.wireOp",EDGE,"E22.left"),sQuery(id+"F0.wireOp",EDGE,"E22.right"),sQuery(id+"F0.wireOp",EDGE,"E26.bottom")])]});
            var Q13;
            Q13=makeQuery(id+"F8.opExtrude","SWEPT_BODY",BODY,{"disambiguationData":[OSD([sQuery(id+"F0.wireOp",EDGE,"E23.bottom"),sQuery(id+"F0.wireOp",EDGE,"E23.left"),sQuery(id+"F0.wireOp",EDGE,"E23.right"),sQuery(id+"F0.wireOp",EDGE,"E27.bottom")])]});
            var Q14;
            Q14=makeQuery(id+"F8.opExtrude","SWEPT_BODY",BODY,{"disambiguationData":[OSD([sQuery(id+"F0.wireOp",EDGE,"E24.bottom"),sQuery(id+"F0.wireOp",EDGE,"E24.left"),sQuery(id+"F0.wireOp",EDGE,"E24.right"),sQuery(id+"F0.wireOp",EDGE,"E28.bottom")])]});
            var Q15;
            Q15=makeQuery(id+"F10.opExtrude","SWEPT_BODY",BODY,{"disambiguationData":[OSD([sQuery(id+"F9.wireOp",EDGE,"E30.bottom"),sQuery(id+"F9.wireOp",EDGE,"E30.top"),sQuery(id+"F9.wireOp",EDGE,"E30.left"),sQuery(id+"F9.wireOp",EDGE,"E30.right"),sQuery(id+"F9.wireOp",EDGE,"E45")])]});
            var Q16;
            Q16=makeQuery(id+"F10.opExtrude","SWEPT_BODY",BODY,{"disambiguationData":[OSD([sQuery(id+"F9.wireOp",EDGE,"E31.bottom"),sQuery(id+"F9.wireOp",EDGE,"E31.top"),sQuery(id+"F9.wireOp",EDGE,"E31.left"),sQuery(id+"F9.wireOp",EDGE,"E31.right"),sQuery(id+"F9.wireOp",EDGE,"E43"),sQuery(id+"F9.wireOp",EDGE,"E49")])]});
            var Q17;
            Q17=makeQuery(id+"F10.opExtrude","SWEPT_BODY",BODY,{"disambiguationData":[OSD([sQuery(id+"F9.wireOp",EDGE,"E32.bottom"),sQuery(id+"F9.wireOp",EDGE,"E32.top"),sQuery(id+"F9.wireOp",EDGE,"E32.left"),sQuery(id+"F9.wireOp",EDGE,"E32.right"),sQuery(id+"F9.wireOp",EDGE,"E51")])]});
            var Q18;
            Q18=makeQuery(id+"F10.opExtrude","SWEPT_BODY",BODY,{"disambiguationData":[OSD([sQuery(id+"F9.wireOp",EDGE,"E37.bottom"),sQuery(id+"F9.wireOp",EDGE,"E37.top"),sQuery(id+"F9.wireOp",EDGE,"E37.left"),sQuery(id+"F9.wireOp",EDGE,"E37.right"),sQuery(id+"F9.wireOp",EDGE,"E47"),sQuery(id+"F9.wireOp",EDGE,"E53")])]});
            var Q19;
            Q19=makeQuery(id+"F5.opExtrude","SWEPT_BODY",BODY,{"disambiguationData":[OSD([sQuery(id+"F0.wireOp",EDGE,"E27.bottom"),sQuery(id+"F0.wireOp",EDGE,"E27.top"),sQuery(id+"F0.wireOp",EDGE,"E27.left"),sQuery(id+"F0.wireOp",EDGE,"E27.right")])]});
            var Q20;
            Q20=sQuery(id+"F0.wireOp",EDGE,"E29");
            transform(context, id + "F12", {"entities" : qUnion([Q0, Q1, Q2, Q3, Q4, Q5, Q6, Q7, Q8, Q9, Q10, Q11, Q12, Q13, Q14, Q15, Q16, Q17, Q18, Q19]), "transformType" : TransformType.ROTATION, "transformAxis" : qUnion([Q20]), "angle" : 180 * degree, "makeCopy" : false});
        }
    });
